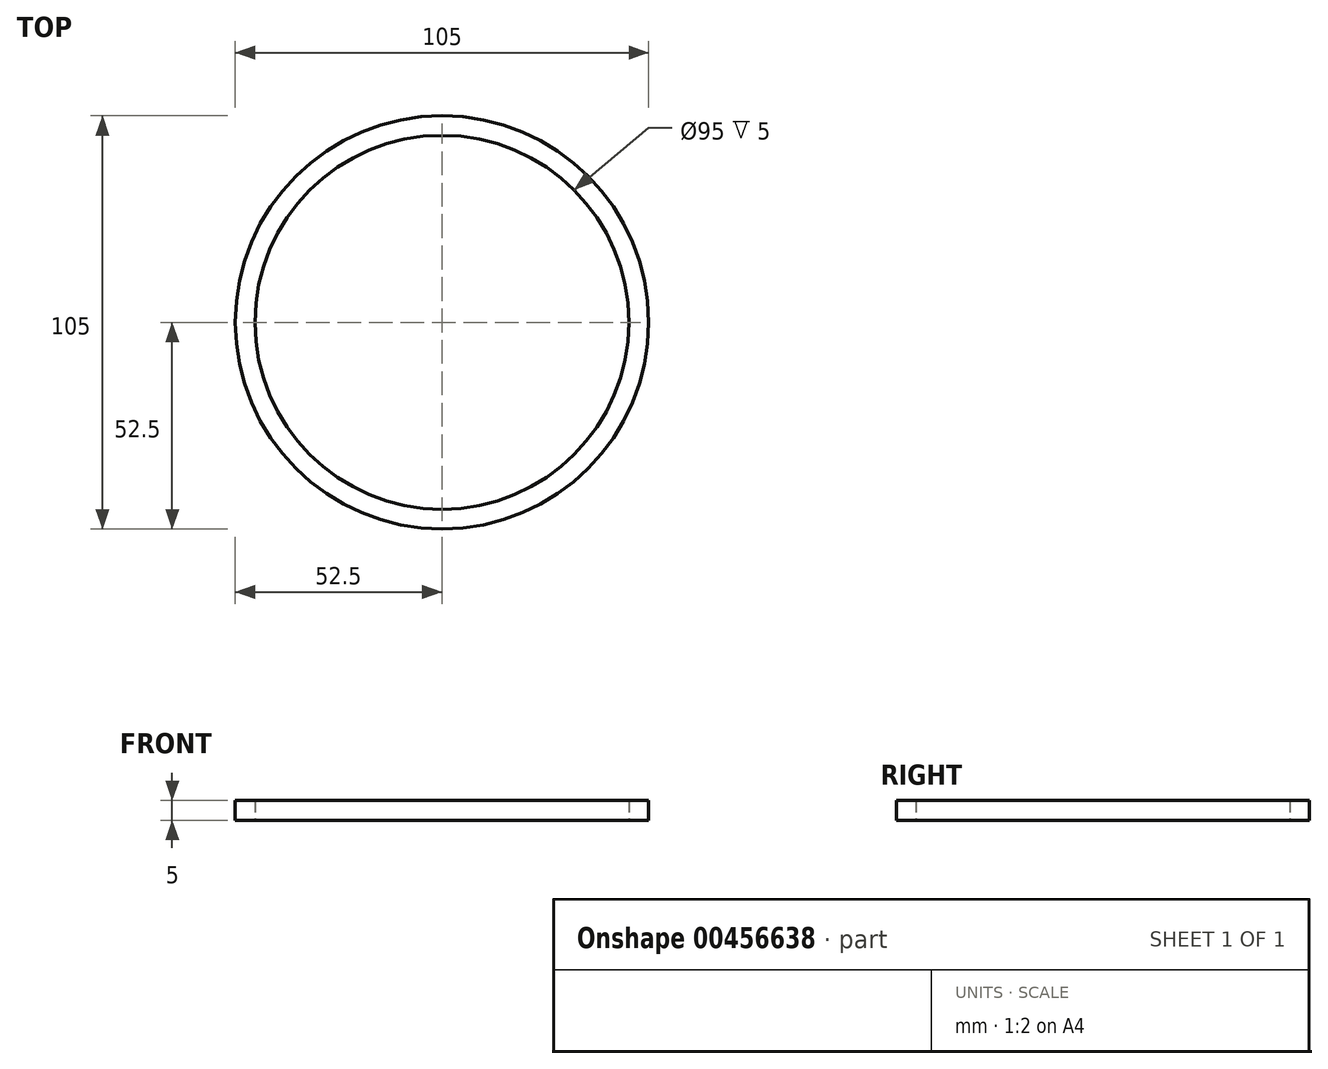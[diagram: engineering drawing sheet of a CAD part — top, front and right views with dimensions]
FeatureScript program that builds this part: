
annotation { "Feature Type Name" : "Feature", "Feature Type Description" : "" }
export const myFeature = defineFeature(function(context is Context, id is Id, definition is map)
    precondition{}
    {
        {
            var Q0;
            Q0=qCreatedBy(makeId("Top.planeOp"),FACE);
            var sketch = newSketch(context, id + "F0", { "sketchPlane" : qUnion([Q0])});
            skCircle(sketch, "E0", {"center": v(0, 0) * mm, "radius": 47.5 * mm});
            skCircle(sketch, "E1.0", {"center": v(0, 0) * mm, "radius": 52.5 * mm});
            skSolve(sketch);
        }
        {
            var Q0;
            Q0=makeQuery(id+"F0.imprint","IMPRINT",FACE,{"disambiguationData":[TD([[makeQuery(id+"F0.imprint","IMPRINT",EDGE,{"derivedFrom":sQuery(id+"F0.wireOp",EDGE,"E0")}),-1.0]])]});
            extrude(context, id + "F1", {"entities" : qUnion([Q0]), "depth" : 5 * mm});
        }
    });
